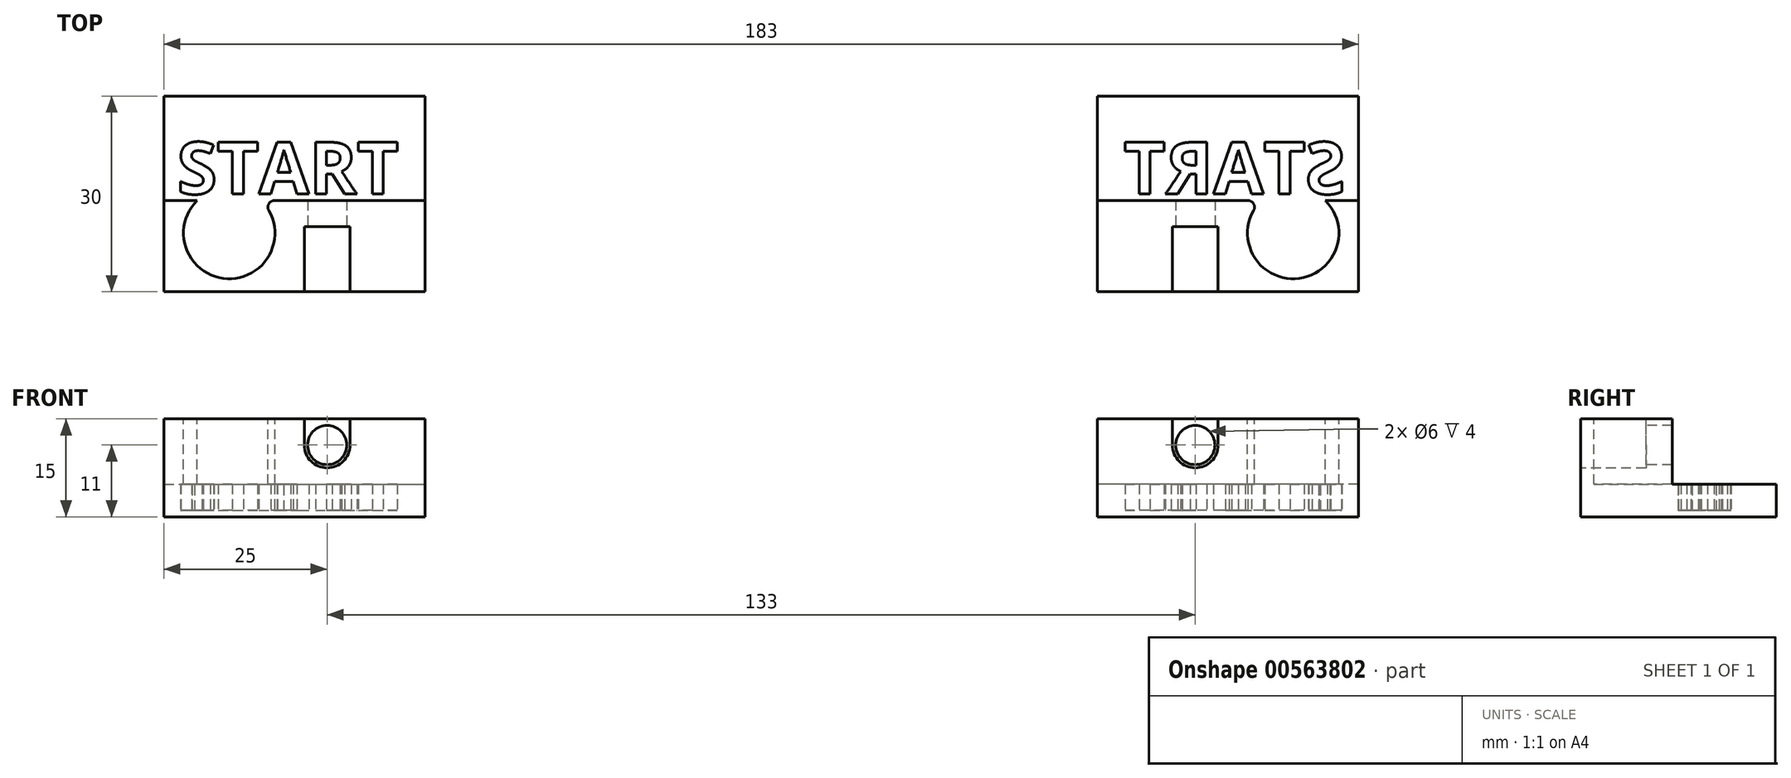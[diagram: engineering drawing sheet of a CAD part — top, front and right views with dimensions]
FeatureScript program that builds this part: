
annotation { "Feature Type Name" : "Feature", "Feature Type Description" : "" }
export const myFeature = defineFeature(function(context is Context, id is Id, definition is map)
    precondition{}
    {
        {
            var Q0;
            Q0=qCreatedBy(makeId("Top.planeOp"),FACE);
            var sketch = newSketch(context, id + "F0", { "sketchPlane" : qUnion([Q0])});
            skLineSegment(sketch, "E0.bottom", {"start": v(-91.5, 40.33) * mm, "end": v(-51.5, 40.33) * mm});
            skLineSegment(sketch, "E0.top", {"start": v(-91.5, 10.33) * mm, "end": v(-51.5, 10.33) * mm});
            skLineSegment(sketch, "E0.left", {"start": v(-91.5, 40.33) * mm, "end": v(-91.5, 10.33) * mm});
            skLineSegment(sketch, "E0.right", {"start": v(-51.5, 40.33) * mm, "end": v(-51.5, 10.33) * mm});
            skSolve(sketch);
        }
        {
            var Q0;
            Q0 = qSketchRegion(id + "F0", true);
            extrude(context, id + "F1", {"entities" : qUnion([Q0]), "depth" : 1 * mm, "offsetDistance" : 25 * mm});
        }
        {
            var Q0;
            Q0=makeQuery(id+"F1.opExtrude","CAP_FACE",FACE,{"disambiguationData":[OSD([sQuery(id+"F0.wireOp",EDGE,"E0.bottom"),sQuery(id+"F0.wireOp",EDGE,"E0.top"),sQuery(id+"F0.wireOp",EDGE,"E0.left"),sQuery(id+"F0.wireOp",EDGE,"E0.right")])],"isStart":false});
            var sketch = newSketch(context, id + "F2", { "sketchPlane" : qUnion([Q0])});
            skLineSegment(sketch, "E1.bottom", {"start": v(-89.5, 33.33) * mm, "end": v(-55.02, 33.33) * mm});
            skLineSegment(sketch, "E1.top", {"start": v(-89.5, 25.33) * mm, "end": v(-55.02, 25.33) * mm});
            skLineSegment(sketch, "E1.left", {"start": v(-89.5, 33.33) * mm, "end": v(-89.5, 25.33) * mm});
            skLineSegment(sketch, "E1.right", {"start": v(-55.02, 33.33) * mm, "end": v(-55.02, 25.33) * mm});
            skText(sketch, "E2", { "text": "START", "fontName": "OpenSans-Bold.ttf"});
            skLineSegment(sketch, "E3", {"start": v(-51.5, 24.33) * mm, "end": v(-91.5, 24.33) * mm});
            const initialGuessF2  = {"E2": [-0.0895, 0.02533, 1, 0, 0.008]};
            skSetInitialGuess(sketch, initialGuessF2);
            skSolve(sketch);
        }
        {
            var Q0;
            {var subQ1=sQuery(id+"F2.wireOp",EDGE,"E1.left");Q0=makeQuery(id+"F2.imprint","IMPRINT",FACE,{"disambiguationData":[TD([[makeQuery(id+"F2.imprint","IMPRINT",EDGE,{"derivedFrom":subQ1}),1.0]])]});}
            var Q1;
            {var subQ12=sQuery(id+"F2.wireOp",EDGE,"E1.right");Q1=makeQuery(id+"F2.imprint","IMPRINT",FACE,{"disambiguationData":[TD([[makeQuery(id+"F2.imprint","IMPRINT",EDGE,{"derivedFrom":subQ12}),-1.0]])]});}
            var Q2;
            Q2=makeQuery(id+"F2.imprint","IMPRINT",FACE,{"disambiguationData":[TD([[makeQuery(id+"F2.imprint","IMPRINT",EDGE,{"derivedFrom":sQuery(id+"F2.wireOp",EDGE,"E2.sketch_text.stroke-44")}),1.0]])]});
            var Q3;
            {var subQ0=sQuery(id+"F2.wireOp",EDGE,"E2.sketch_text.stroke-36");Q3=makeQuery(id+"F2.imprint","IMPRINT",FACE,{"disambiguationData":[TD([[makeQuery(id+"F2.imprint","IMPRINT",EDGE,{"derivedFrom":subQ0}),1.0]])]});}
            var Q4;
            Q4=makeQuery(id+"F2.imprint","IMPRINT",FACE,{"disambiguationData":[TD([[makeQuery(id+"F2.imprint","IMPRINT",EDGE,{"derivedFrom":sQuery(id+"F2.wireOp",EDGE,"E2.sketch_text.stroke-48")}),1.0]])]});
            var Q5;
            {var subQ0=sQuery(id+"F2.wireOp",EDGE,"E2.sketch_text.stroke-55");Q5=makeQuery(id+"F2.imprint","IMPRINT",FACE,{"disambiguationData":[TD([[makeQuery(id+"F2.imprint","IMPRINT",EDGE,{"derivedFrom":subQ0}),1.0]])]});}
            extrude(context, id + "F3", {"entities" : qUnion([Q0, Q1, Q2, Q3, Q4, Q5]), "operationType" : NewBodyOperationType.ADD, "depth" : 4 * mm, "offsetDistance" : 25 * mm});
        }
        {
            var Q0;
            {var subQ10=sQuery(id+"F2.wireOp",EDGE,"E1.left");Q0=makeQuery(id+"F2.imprint","IMPRINT",FACE,{"disambiguationData":[TD([[makeQuery(id+"F2.imprint","IMPRINT",EDGE,{"derivedFrom":subQ10}),-1.0]])]});}
            var Q1;
            {var subQ13=makeQuery(id+"F1.opExtrude","CAP_EDGE",EDGE,{"disambiguationData":[OSD([sQuery(id+"F0.wireOp",EDGE,"E0.top")])],"isStart":false});Q1=makeQuery(id+"F2.imprint","IMPRINT",FACE,{"disambiguationData":[TD([[makeQuery(id+"F2.imprint","IMPRINT",EDGE,{"derivedFrom":subQ13}),1.0]])]});}
            extrude(context, id + "F4", {"entities" : qUnion([Q0, Q1]), "operationType" : NewBodyOperationType.ADD, "depth" : 4 * mm, "offsetDistance" : 25 * mm});
        }
        {
            var Q0;
            {var subQ13=makeQuery(id+"F1.opExtrude","CAP_EDGE",EDGE,{"disambiguationData":[OSD([sQuery(id+"F0.wireOp",EDGE,"E0.top")])],"isStart":false});Q0=makeQuery(id+"F2.imprint","IMPRINT",FACE,{"disambiguationData":[TD([[makeQuery(id+"F2.imprint","IMPRINT",EDGE,{"derivedFrom":subQ13}),1.0]])]});}
            extrude(context, id + "F5", {"entities" : qUnion([Q0]), "operationType" : NewBodyOperationType.ADD, "depth" : 14 * mm, "offsetDistance" : 25 * mm});
        }
        {
            var Q0;
            {var subQ0=sQuery(id+"F0.wireOp",EDGE,"E0.top");Q0=makeQuery(id+"F5.boolean.opBoolean","MERGE",FACE,{"derivedFrom":[makeQuery(id+"F4.boolean.opBoolean","MERGE",FACE,{"derivedFrom":[makeQuery(id+"F1.opExtrude","SWEPT_FACE",FACE,{"disambiguationData":[OSD([subQ0])]}),makeQuery(id+"F4.opExtrude","SWEPT_FACE",FACE,{"disambiguationData":[OSD([subQ0])]})]}),makeQuery(id+"F5.opExtrude","SWEPT_FACE",FACE,{"disambiguationData":[OSD([subQ0])]})]});}
            var sketch = newSketch(context, id + "F6", { "sketchPlane" : qUnion([Q0])});
            skCircle(sketch, "E4", {"center": v(-66.5, 11) * mm, "radius": 3 * mm});
            skArc(sketch, "E5", {"start": v(-70, 11) * mm, "mid": v(-66.5, 7.5) * mm, "end": v(-63, 11) * mm});
            skLineSegment(sketch, "E6", {"start": v(-63, 11) * mm, "end": v(-63, 15) * mm});
            skLineSegment(sketch, "E7", {"start": v(-70, 11) * mm, "end": v(-70, 15) * mm});
            skSolve(sketch);
        }
        {
            var Q0;
            Q0=makeQuery(id+"F6.imprint","IMPRINT",FACE,{"disambiguationData":[TD([[makeQuery(id+"F6.imprint","IMPRINT",EDGE,{"derivedFrom":sQuery(id+"F6.wireOp",EDGE,"E4")}),1.0]])]});
            extrude(context, id + "F7", {"entities" : qUnion([Q0]), "operationType" : NewBodyOperationType.REMOVE, "oppositeDirection" : true, "depth" : 14 * mm, "offsetDistance" : 25 * mm});
        }
        {
            var Q0;
            Q0=makeQuery(id+"F5.opExtrude","CAP_FACE",FACE,{"disambiguationData":[OSD([sQuery(id+"F0.wireOp",EDGE,"E0.top"),sQuery(id+"F0.wireOp",EDGE,"E0.left"),sQuery(id+"F0.wireOp",EDGE,"E0.right"),sQuery(id+"F2.wireOp",EDGE,"E3")])],"isStart":false});
            var sketch = newSketch(context, id + "F8", { "sketchPlane" : qUnion([Q0])});
            skCircle(sketch, "E8", {"center": v(-81.5, 19.33) * mm, "radius": 7 * mm});
            skSolve(sketch);
        }
        {
            var Q0;
            {var subQ0=sQuery(id+"F8.wireOp",EDGE,"E8");var subQ1=makeQuery(id+"F5.opExtrude","CAP_EDGE",EDGE,{"disambiguationData":[OSD([sQuery(id+"F2.wireOp",EDGE,"E3")])],"isStart":false});var subQ2=makeQuery(id+"F8.imprint","INTERSECT",VERTEX,{"disambiguationData":[OD(0.0)],"derivedFrom":[subQ1,subQ0]});Q0=makeQuery(id+"F8.imprint","IMPRINT",FACE,{"disambiguationData":[TD([[makeQuery(id+"F8.imprint","IMPRINT",EDGE,{"disambiguationData":[TD([[subQ2,1.0]])],"derivedFrom":subQ0}),1.0]])]});}
            extrude(context, id + "F9", {"entities" : qUnion([Q0]), "operationType" : NewBodyOperationType.REMOVE, "oppositeDirection" : true, "depth" : 10 * mm, "offsetDistance" : 25 * mm});
        }
        {
            var Q0;
            {var subQ0=sQuery(id+"F8.wireOp",EDGE,"E8");var subQ1=sQuery(id+"F2.wireOp",EDGE,"E3");Q0=makeQuery(id+"F9.boolean.opBoolean","COPY",EDGE,{"derivedFrom":makeQuery(id+"F9.opExtrude","SWEPT_EDGE",EDGE,{"disambiguationData":[OSD([subQ1,subQ0]),TDD([makeQuery(id+"F8.imprint","INTERSECT",VERTEX,{"disambiguationData":[OD(0.0)],"derivedFrom":[makeQuery(id+"F5.opExtrude","CAP_EDGE",EDGE,{"disambiguationData":[OSD([subQ1])],"isStart":false}),subQ0]})])]})});}
            var Q1;
            {var subQ0=sQuery(id+"F8.wireOp",EDGE,"E8");var subQ1=sQuery(id+"F2.wireOp",EDGE,"E3");Q1=makeQuery(id+"F9.boolean.opBoolean","COPY",EDGE,{"derivedFrom":makeQuery(id+"F9.opExtrude","SWEPT_EDGE",EDGE,{"disambiguationData":[OSD([subQ1,subQ0]),TDD([makeQuery(id+"F8.imprint","INTERSECT",VERTEX,{"disambiguationData":[OD(1.0)],"derivedFrom":[makeQuery(id+"F5.opExtrude","CAP_EDGE",EDGE,{"disambiguationData":[OSD([subQ1])],"isStart":false}),subQ0]})])]})});}
            fillet(context, id + "F10", {"entities" : qUnion([Q0, Q1]), "radius" : 1 * mm, "tangentPropagation" : true, "allowEdgeOverflow" : false});
        }
        {
            var Q0;
            Q0=makeQuery(id+"F6.imprint","IMPRINT",FACE,{"disambiguationData":[TD([[makeQuery(id+"F6.imprint","IMPRINT",EDGE,{"derivedFrom":sQuery(id+"F6.wireOp",EDGE,"E4")}),-1.0]])]});
            var Q1;
            Q1=sQuery(id+"F6.wireOp",EDGE,"E5");
            extrude(context, id + "F11", {"entities" : qUnion([Q0]), "operationType" : NewBodyOperationType.REMOVE, "surfaceEntities" : qUnion([Q1]), "oppositeDirection" : true, "depth" : 10 * mm, "offsetDistance" : 25 * mm});
        }
        {
            var Q0;
            Q0=makeQuery(id+"F1.opExtrude","SWEPT_BODY",BODY,{"disambiguationData":[OSD([sQuery(id+"F0.wireOp",EDGE,"E0.bottom"),sQuery(id+"F0.wireOp",EDGE,"E0.top"),sQuery(id+"F0.wireOp",EDGE,"E0.left"),sQuery(id+"F0.wireOp",EDGE,"E0.right")])]});
            var Q1;
            Q1=qCreatedBy(makeId("Right.planeOp"),FACE);
            mirror(context, id + "F12", {"entities" : qUnion([Q0]), "mirrorPlane" : qUnion([Q1])});
        }
    });
